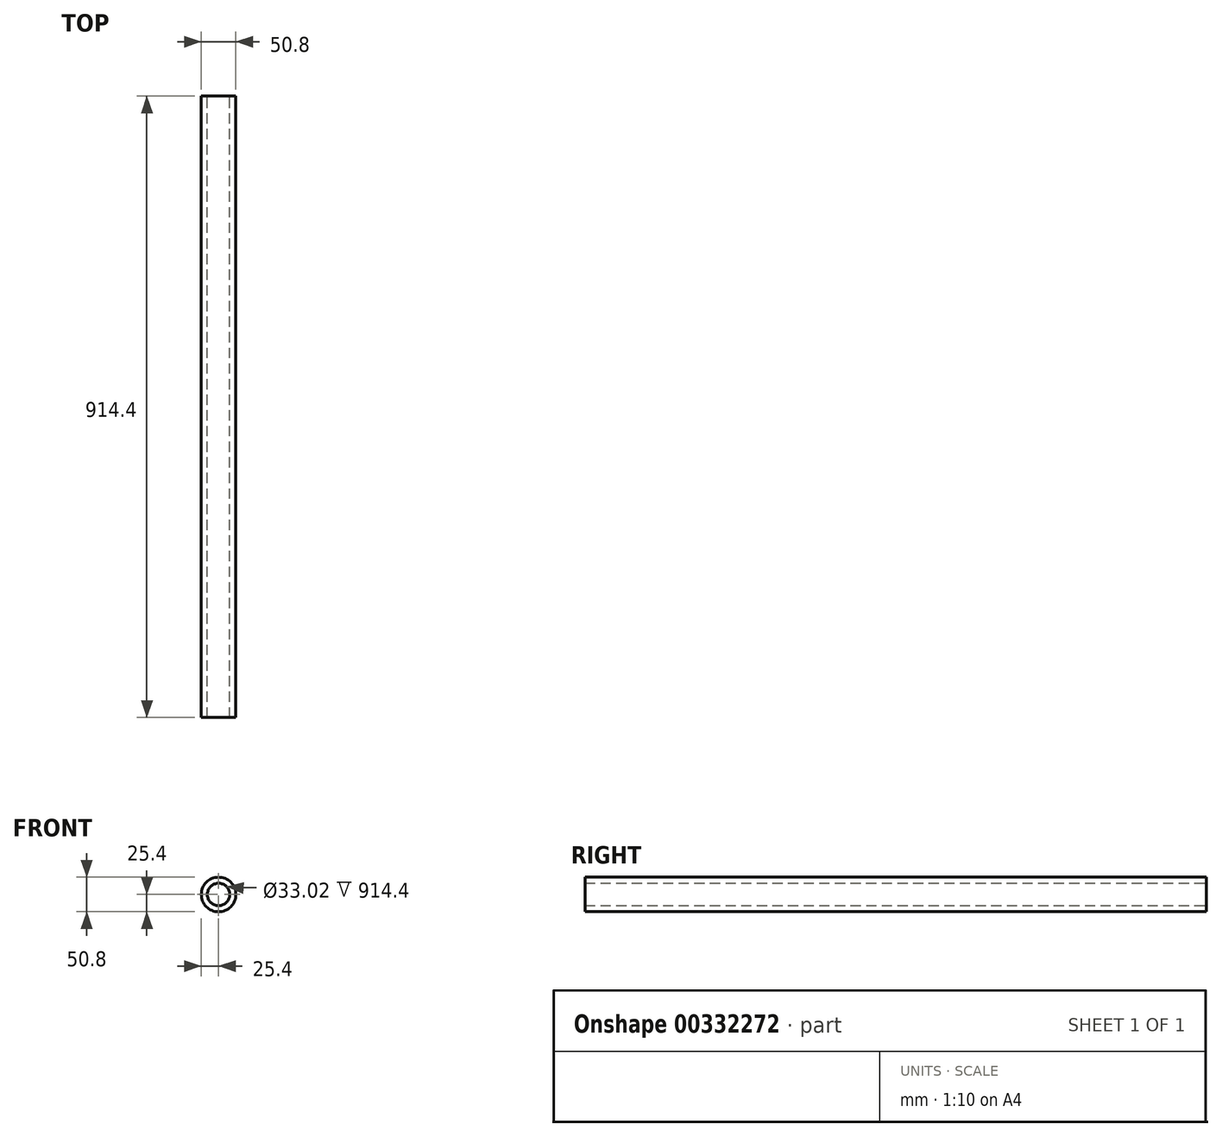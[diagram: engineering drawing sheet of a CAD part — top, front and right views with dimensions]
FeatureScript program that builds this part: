
annotation { "Feature Type Name" : "Feature", "Feature Type Description" : "" }
export const myFeature = defineFeature(function(context is Context, id is Id, definition is map)
    precondition{}
    {
        {
            var Q0;
            Q0=qCreatedBy(makeId("Front.planeOp"),FACE);
            var sketch = newSketch(context, id + "F0", { "sketchPlane" : qUnion([Q0])});
            skCircle(sketch, "E0", {"center": v(0, 0) * mm, "radius": 25.4 * mm});
            skCircle(sketch, "E1", {"center": v(0, 0) * mm, "radius": 16.51 * mm});
            skSolve(sketch);
        }
        {
            var Q0;
            Q0 = qSketchRegion(id + "F0", true);
            extrude(context, id + "F1", {"entities" : qUnion([Q0]), "depth" : 914.4 * mm});
        }
    });
